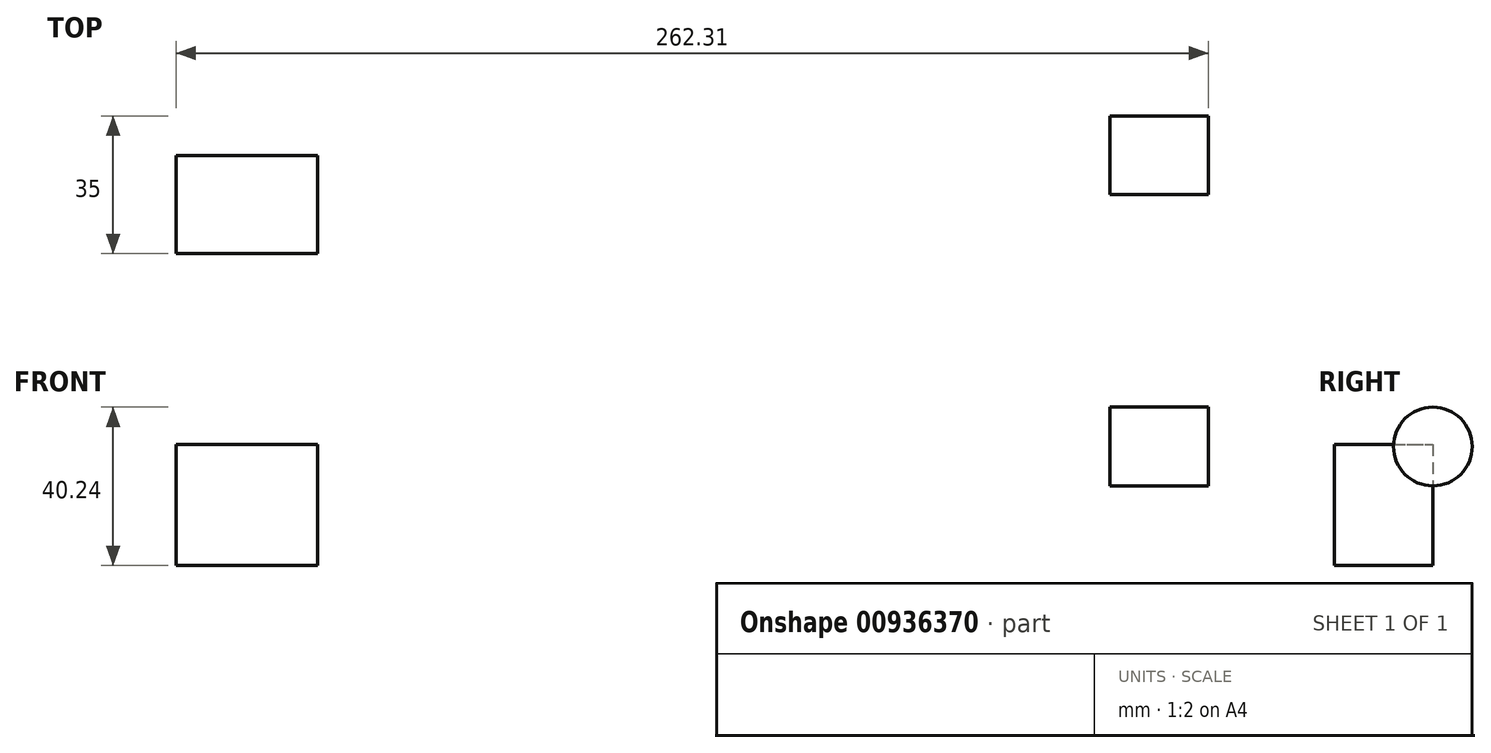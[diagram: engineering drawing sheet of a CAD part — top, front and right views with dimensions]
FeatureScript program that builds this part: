
annotation { "Feature Type Name" : "Feature", "Feature Type Description" : "" }
export const myFeature = defineFeature(function(context is Context, id is Id, definition is map)
    precondition{}
    {
        {
            var Q0;
            Q0=qCreatedBy(makeId("Front.planeOp"),FACE);
            var sketch = newSketch(context, id + "F0", { "sketchPlane" : qUnion([Q0])});
            skLineSegment(sketch, "E0.bottom", {"start": v(-112.46, 56.3) * mm, "end": v(-76.43, 56.3) * mm});
            skLineSegment(sketch, "E0.top", {"start": v(-112.46, 25.48) * mm, "end": v(-76.43, 25.48) * mm});
            skLineSegment(sketch, "E0.left", {"start": v(-112.46, 56.3) * mm, "end": v(-112.46, 25.48) * mm});
            skLineSegment(sketch, "E0.right", {"start": v(-76.43, 56.3) * mm, "end": v(-76.43, 25.48) * mm});
            skSolve(sketch);
        }
        {
            var Q0;
            Q0=makeQuery(id+"F0.imprint","IMPRINT",FACE,{"disambiguationData":[TD([[makeQuery(id+"F0.imprint","IMPRINT",EDGE,{"derivedFrom":sQuery(id+"F0.wireOp",EDGE,"E0.bottom")}),-1.0]])]});
            extrude(context, id + "F1", {"entities" : qUnion([Q0]), "depth" : 25 * mm, "offsetDistance" : 25 * mm});
        }
        {
            var Q0;
            Q0=qCreatedBy(makeId("Front.planeOp"),FACE);
            var sketch = newSketch(context, id + "F2", { "sketchPlane" : qUnion([Q0])});
            skLineSegment(sketch, "E1.bottom", {"start": v(124.85, 65.72) * mm, "end": v(149.85, 65.72) * mm});
            skLineSegment(sketch, "E1.top", {"start": v(124.85, 55.72) * mm, "end": v(149.85, 55.72) * mm});
            skLineSegment(sketch, "E1.left", {"start": v(124.85, 65.72) * mm, "end": v(124.85, 55.72) * mm});
            skLineSegment(sketch, "E1.right", {"start": v(149.85, 65.72) * mm, "end": v(149.85, 55.72) * mm});
            skSolve(sketch);
        }
        {
            var Q0;
            Q0=makeQuery(id+"F2.imprint","IMPRINT",FACE,{"disambiguationData":[TD([[makeQuery(id+"F2.imprint","IMPRINT",EDGE,{"derivedFrom":sQuery(id+"F2.wireOp",EDGE,"E1.bottom")}),-1.0]])]});
            var Q1;
            Q1=sQuery(id+"F2.wireOp",EDGE,"E1.top");
            revolve(context, id + "F3", {"surfaceOperationType" : NewSurfaceOperationType.NEW, "entities" : qUnion([Q0]), "axis" : qUnion([Q1]), "revolveType" : RevolveType.FULL});
        }
    });
